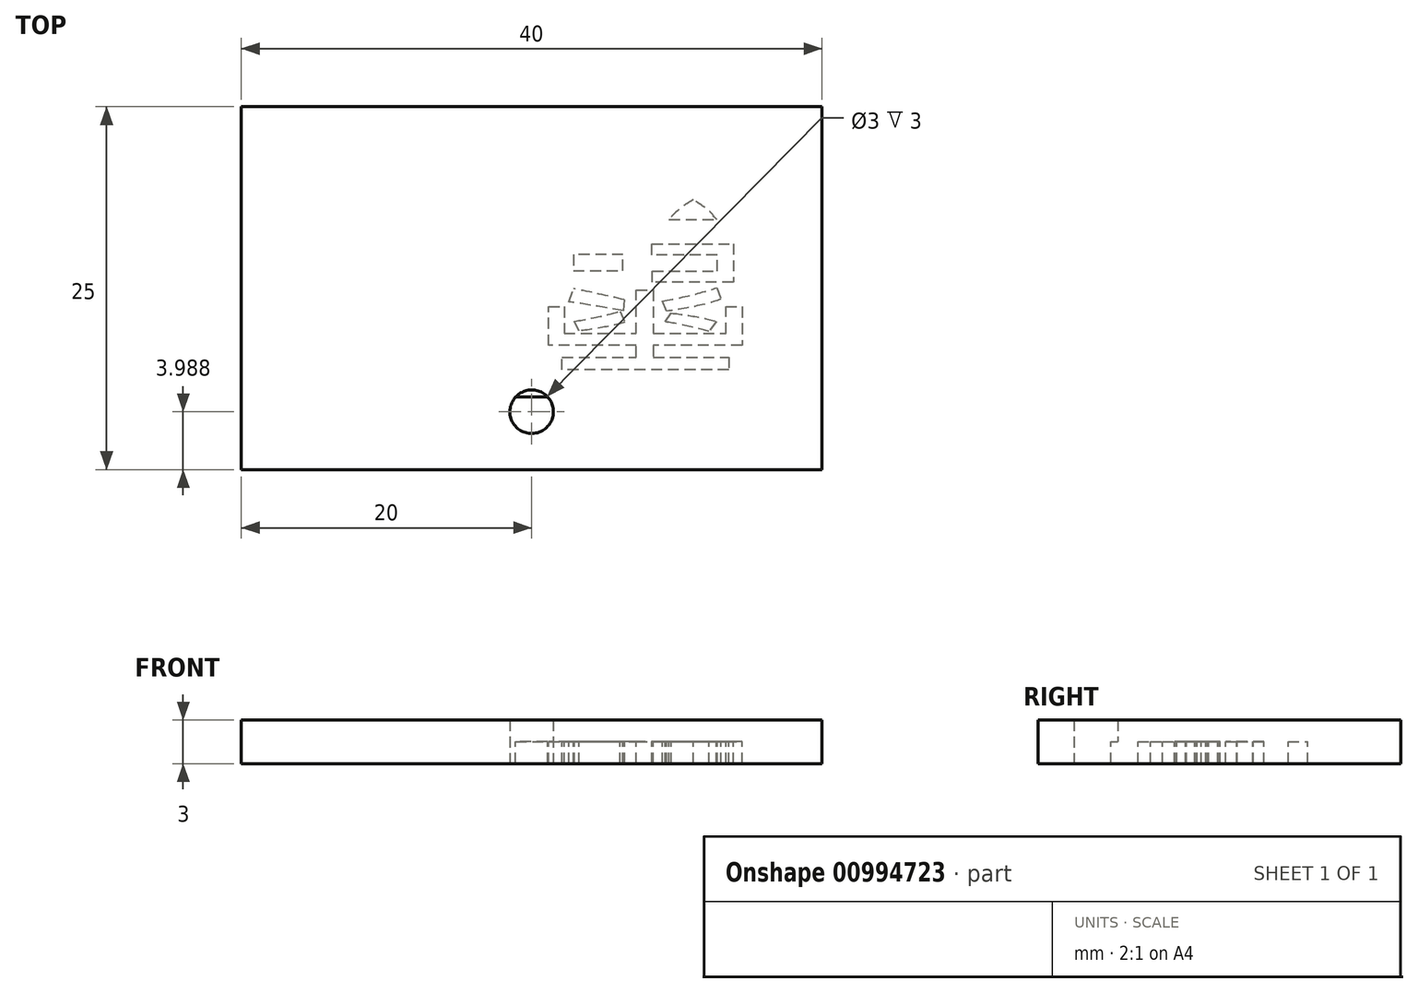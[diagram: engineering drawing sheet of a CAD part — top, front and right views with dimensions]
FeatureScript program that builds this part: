
annotation { "Feature Type Name" : "Feature", "Feature Type Description" : "" }
export const myFeature = defineFeature(function(context is Context, id is Id, definition is map)
    precondition{}
    {
        {
            var Q0;
            Q0=qCreatedBy(makeId("Top.planeOp"),FACE);
            var sketch = newSketch(context, id + "F0", { "sketchPlane" : qUnion([Q0])});
            skLineSegment(sketch, "E0.bottom", {"start": v(20, -12.5) * mm, "end": v(-20, -12.5) * mm});
            skLineSegment(sketch, "E0.top", {"start": v(20, 12.5) * mm, "end": v(-20, 12.5) * mm});
            skLineSegment(sketch, "E0.left", {"start": v(20, -12.5) * mm, "end": v(20, 12.5) * mm});
            skLineSegment(sketch, "E0.right", {"start": v(-20, -12.5) * mm, "end": v(-20, 12.5) * mm});
            skPoint(sketch, "E0.middle", {"position": v(0, 0) * mm});
            skSolve(sketch);
        }
        {
            var Q0;
            Q0 = qSketchRegion(id + "F0", true);
            extrude(context, id + "F1", {"entities" : qUnion([Q0]), "depth" : 3 * mm, "offsetDistance" : 25 * mm});
        }
        {
            var Q0;
            Q0=qCreatedBy(makeId("Top.planeOp"),FACE);
            var sketch = newSketch(context, id + "F2", { "sketchPlane" : qUnion([Q0])});
            skLineSegment(sketch, "E1.0", {"start": v(18, -10.5) * mm, "end": v(18, 10.5) * mm});
            skLineSegment(sketch, "E1.1", {"start": v(-18, -10.5) * mm, "end": v(18, -10.5) * mm});
            skLineSegment(sketch, "E1.2", {"start": v(-18, 10.5) * mm, "end": v(-18, -10.5) * mm});
            skLineSegment(sketch, "E1.3", {"start": v(18, 10.5) * mm, "end": v(-18, 10.5) * mm});
            skSolve(sketch);
        }
        {
            var Q0;
            Q0 = qSketchRegion(id + "F2", true);
            extrude(context, id + "F3", {"entities" : qUnion([Q0]), "operationType" : NewBodyOperationType.REMOVE, "depth" : 1.5 * mm, "offsetDistance" : 25 * mm});
        }
        {
            var Q0;
            Q0=makeQuery(id+"F3.boolean.opBoolean","COPY",FACE,{"derivedFrom":makeQuery(id+"F3.opExtrude","CAP_FACE",FACE,{"disambiguationData":[OSD([sQuery(id+"F2.wireOp",EDGE,"E1.0"),sQuery(id+"F2.wireOp",EDGE,"E1.1"),sQuery(id+"F2.wireOp",EDGE,"E1.2"),sQuery(id+"F2.wireOp",EDGE,"E1.3")])],"isStart":false})});
            var sketch = newSketch(context, id + "F4", { "sketchPlane" : qUnion([Q0])});
            skCircle(sketch, "E2", {"center": v(0, 8.51) * mm, "radius": 1.5 * mm});
            skSolve(sketch);
        }
        {
            var Q0;
            Q0 = qSketchRegion(id + "F4", true);
            extrude(context, id + "F5", {"entities" : qUnion([Q0]), "operationType" : NewBodyOperationType.REMOVE, "endBound" : BoundingType.THROUGH_ALL, "oppositeDirection" : true, "depth" : 25 * mm, "offsetDistance" : 25 * mm});
        }
        {
            var Q0;
            Q0=makeQuery(id+"F3.boolean.opBoolean","COPY",FACE,{"derivedFrom":makeQuery(id+"F3.opExtrude","CAP_FACE",FACE,{"disambiguationData":[OSD([sQuery(id+"F2.wireOp",EDGE,"E1.0"),sQuery(id+"F2.wireOp",EDGE,"E1.1"),sQuery(id+"F2.wireOp",EDGE,"E1.2"),sQuery(id+"F2.wireOp",EDGE,"E1.3")])],"isStart":false})});
            var sketch = newSketch(context, id + "F6", { "sketchPlane" : qUnion([Q0])});
            skText(sketch, "E3", { "text": "秀霞", "fontName": "NotoSansCJKtc-Regular.otf"});
            skLineSegment(sketch, "E4.0", {"start": v(15, -7.5) * mm, "end": v(15, 7.5) * mm});
            skLineSegment(sketch, "E4.1", {"start": v(-15, -7.5) * mm, "end": v(15, -7.5) * mm});
            skLineSegment(sketch, "E4.2", {"start": v(-15, 7.5) * mm, "end": v(-15, -7.5) * mm});
            skLineSegment(sketch, "E4.3", {"start": v(15, 7.5) * mm, "end": v(-15, 7.5) * mm});
            const initialGuessF6  = {"E3": [-0.016, -0.00702, 1, 0, 0.01144]};
            skSetInitialGuess(sketch, initialGuessF6);
            skSolve(sketch);
        }
        {
            var Q0;
            Q0 = qSketchRegion(id + "F6", true);
            var Q1;
            {var subQ27=sQuery(id+"F6.wireOp",EDGE,"E3.sketch_text.stroke-14");Q1=makeQuery(id+"F6.imprint","IMPRINT",FACE,{"disambiguationData":[TD([[makeQuery(id+"F6.imprint","IMPRINT",EDGE,{"derivedFrom":subQ27}),-1.0]])]});}
            extrude(context, id + "F7", {"entities" : qUnion([Q0, Q1]), "operationType" : NewBodyOperationType.ADD, "depth" : 1.5 * mm, "offsetDistance" : 25 * mm});
        }
    });
